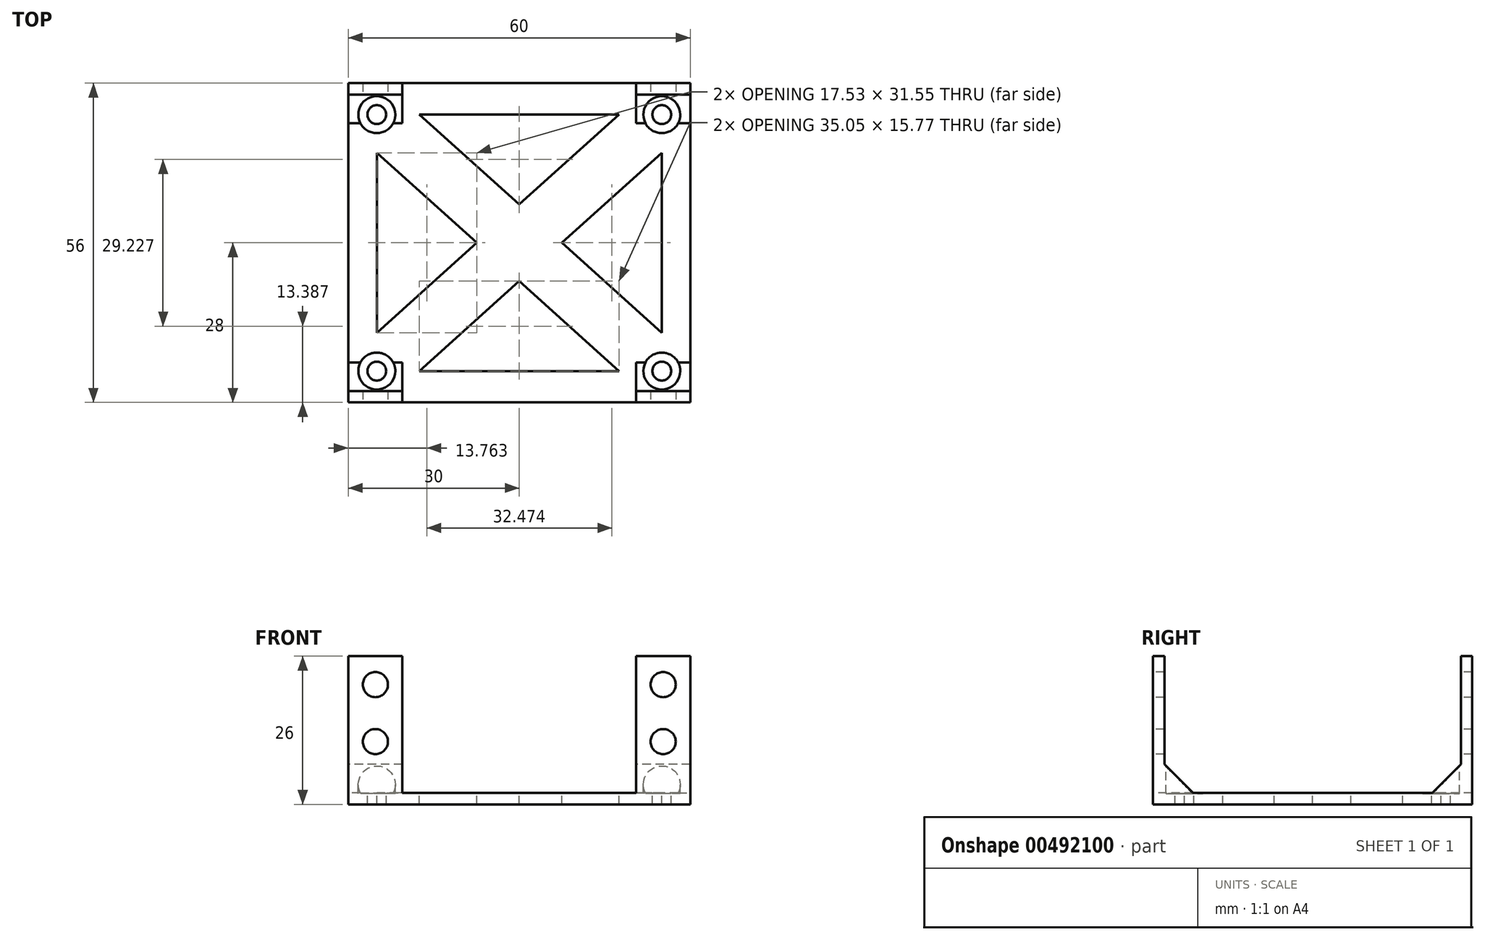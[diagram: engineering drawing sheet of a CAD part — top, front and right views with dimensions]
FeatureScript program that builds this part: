
annotation { "Feature Type Name" : "Feature", "Feature Type Description" : "" }
export const myFeature = defineFeature(function(context is Context, id is Id, definition is map)
    precondition{}
    {
        {
            var Q0;
            Q0=qCreatedBy(makeId("Top.planeOp"),FACE);
            var sketch = newSketch(context, id + "F0", { "sketchPlane" : qUnion([Q0])});
            skLineSegment(sketch, "E0.bottom", {"start": v(-30, 28) * mm, "end": v(30, 28) * mm});
            skLineSegment(sketch, "E0.top", {"start": v(-30, -28) * mm, "end": v(30, -28) * mm});
            skLineSegment(sketch, "E0.left", {"start": v(-30, 28) * mm, "end": v(-30, -28) * mm});
            skLineSegment(sketch, "E0.right", {"start": v(30, 28) * mm, "end": v(30, -28) * mm});
            skSolve(sketch);
        }
        {
            var Q0;
            Q0=makeQuery(id+"F0.imprint","IMPRINT",FACE,{"disambiguationData":[TD([[makeQuery(id+"F0.imprint","IMPRINT",EDGE,{"derivedFrom":sQuery(id+"F0.wireOp",EDGE,"E0.bottom")}),-1.0]])]});
            extrude(context, id + "F1", {"entities" : qUnion([Q0]), "depth" : 26 * mm});
        }
        {
            var Q0;
            Q0=makeQuery(id+"F1.opExtrude","SWEPT_FACE",FACE,{"disambiguationData":[OSD([sQuery(id+"F0.wireOp",EDGE,"E0.top")])]});
            var sketch = newSketch(context, id + "F2", { "sketchPlane" : qUnion([Q0])});
            skLineSegment(sketch, "E1.bottom", {"start": v(-20.5, 26) * mm, "end": v(20.5, 26) * mm});
            skLineSegment(sketch, "E1.top", {"start": v(-20.5, 2) * mm, "end": v(20.5, 2) * mm});
            skLineSegment(sketch, "E1.left", {"start": v(-20.5, 26) * mm, "end": v(-20.5, 2) * mm});
            skLineSegment(sketch, "E1.right", {"start": v(20.5, 26) * mm, "end": v(20.5, 2) * mm});
            skSolve(sketch);
        }
        {
            var Q0;
            Q0=makeQuery(id+"F2.imprint","IMPRINT",FACE,{"disambiguationData":[TD([[makeQuery(id+"F2.imprint","IMPRINT",EDGE,{"derivedFrom":sQuery(id+"F2.wireOp",EDGE,"E1.bottom")}),-1.0]])]});
            extrude(context, id + "F3", {"entities" : qUnion([Q0]), "operationType" : NewBodyOperationType.REMOVE, "endBound" : BoundingType.THROUGH_ALL, "oppositeDirection" : true, "depth" : 25 * mm});
        }
        {
            var Q0;
            Q0=makeQuery(id+"F1.opExtrude","SWEPT_FACE",FACE,{"disambiguationData":[OSD([sQuery(id+"F0.wireOp",EDGE,"E0.right")])]});
            var sketch = newSketch(context, id + "F4", { "sketchPlane" : qUnion([Q0])});
            skLineSegment(sketch, "E2.bottom", {"start": v(-26, 26) * mm, "end": v(26, 26) * mm});
            skLineSegment(sketch, "E2.top", {"start": v(-26, 2) * mm, "end": v(26, 2) * mm});
            skLineSegment(sketch, "E2.left", {"start": v(-26, 26) * mm, "end": v(-26, 2) * mm});
            skLineSegment(sketch, "E2.right", {"start": v(26, 26) * mm, "end": v(26, 2) * mm});
            skSolve(sketch);
        }
        {
            var Q0;
            Q0=makeQuery(id+"F4.imprint","IMPRINT",FACE,{"disambiguationData":[TD([[makeQuery(id+"F4.imprint","IMPRINT",EDGE,{"derivedFrom":sQuery(id+"F4.wireOp",EDGE,"E2.bottom")}),1.0]])]});
            extrude(context, id + "F5", {"entities" : qUnion([Q0]), "operationType" : NewBodyOperationType.REMOVE, "endBound" : BoundingType.THROUGH_ALL, "oppositeDirection" : true, "depth" : 25 * mm});
        }
        {
            var Q0;
            Q0=makeQuery(id+"F1.opExtrude","SWEPT_FACE",FACE,{"disambiguationData":[OSD([sQuery(id+"F0.wireOp",EDGE,"E0.top")])]});
            var sketch = newSketch(context, id + "F6", { "sketchPlane" : qUnion([Q0])});
            skPoint(sketch, "E3", {"position": v(-25.25, 21) * mm});
            skPoint(sketch, "E4", {"position": v(-25.25, 11) * mm});
            skPoint(sketch, "E5", {"position": v(25.25, 21) * mm});
            skPoint(sketch, "E6", {"position": v(25.25, 11) * mm});
            skSolve(sketch);
        }
        {
            var Q0;
            Q0=sQuery(id+"F6.wireOp",VERTEX,"E3");
            var Q1;
            Q1=sQuery(id+"F6.wireOp",VERTEX,"E5");
            var Q2;
            Q2=sQuery(id+"F6.wireOp",VERTEX,"E6");
            var Q3;
            Q3=sQuery(id+"F6.wireOp",VERTEX,"E4");
            var Q4;
            Q4=makeQuery(id+"F1.opExtrude","SWEPT_BODY",BODY,{"disambiguationData":[OSD([sQuery(id+"F0.wireOp",EDGE,"E0.bottom"),sQuery(id+"F0.wireOp",EDGE,"E0.top"),sQuery(id+"F0.wireOp",EDGE,"E0.left"),sQuery(id+"F0.wireOp",EDGE,"E0.right")])]});
            hole(context, id + "F7", {"style" : HoleStyle.SIMPLE, "endStyle" : HoleEndStyle.THROUGH, "standardTappedOrClearance" : lookupTablePath({ "standard" : "ISO", "fit" : "Normal", "size" : "M4", "type" : "Clearance" }), "standardBlindInLast" : lookupTablePath({ "fit" : "Standard", "standard" : "ISO", "size" : "M4", "type" : "Clearance" }), "holeDiameter" : 4.4 * mm, "isTappedThrough" : true, "tappedDepth" : 12 * mm, "tapClearance" : 3, "locations" : qUnion([Q0, Q1, Q2, Q3]), "scope" : qUnion([Q4])});
        }
        {
            var Q0;
            Q0=makeQuery(id+"F5.boolean.opBoolean","MERGE",FACE,{"derivedFrom":[makeQuery(id+"F3.boolean.opBoolean","COPY",FACE,{"derivedFrom":makeQuery(id+"F3.opExtrude","SWEPT_FACE",FACE,{"disambiguationData":[OSD([sQuery(id+"F2.wireOp",EDGE,"E1.top")])]})}),makeQuery(id+"F5.opExtrude","SWEPT_FACE",FACE,{"disambiguationData":[OSD([sQuery(id+"F4.wireOp",EDGE,"E2.top")])]})]});
            var sketch = newSketch(context, id + "F8", { "sketchPlane" : qUnion([Q0])});
            skPoint(sketch, "E7", {"position": v(25, 22.5) * mm});
            skPoint(sketch, "E8", {"position": v(-25, 22.5) * mm});
            skPoint(sketch, "E9", {"position": v(25, -22.5) * mm});
            skPoint(sketch, "E10", {"position": v(-25, -22.5) * mm});
            skSolve(sketch);
        }
        {
            var Q0;
            Q0=sQuery(id+"F8.wireOp",VERTEX,"E9");
            var Q1;
            Q1=sQuery(id+"F8.wireOp",VERTEX,"E10");
            var Q2;
            Q2=sQuery(id+"F8.wireOp",VERTEX,"E7");
            var Q3;
            Q3=sQuery(id+"F8.wireOp",VERTEX,"E8");
            var Q4;
            Q4=makeQuery(id+"F1.opExtrude","SWEPT_BODY",BODY,{"disambiguationData":[OSD([sQuery(id+"F0.wireOp",EDGE,"E0.bottom"),sQuery(id+"F0.wireOp",EDGE,"E0.top"),sQuery(id+"F0.wireOp",EDGE,"E0.left"),sQuery(id+"F0.wireOp",EDGE,"E0.right")])]});
            hole(context, id + "F9", {"style" : HoleStyle.C_BORE, "endStyle" : HoleEndStyle.BLIND, "holeDiameter" : 3.3 * mm, "cBoreDiameter" : 6.5 * mm, "cBoreDepth" : .1 * mm, "holeDepth" : 12 * mm, "isTappedThrough" : true, "tappedDepth" : 12 * mm, "tapClearance" : 3, "startFromSketch" : true, "locations" : qUnion([Q0, Q1, Q2, Q3]), "scope" : qUnion([Q4])});
        }
        {
            var Q0;
            Q0=makeQuery(id+"F5.boolean.opBoolean","MERGE",FACE,{"derivedFrom":[makeQuery(id+"F3.boolean.opBoolean","COPY",FACE,{"derivedFrom":makeQuery(id+"F3.opExtrude","SWEPT_FACE",FACE,{"disambiguationData":[OSD([sQuery(id+"F2.wireOp",EDGE,"E1.top")])]})}),makeQuery(id+"F5.opExtrude","SWEPT_FACE",FACE,{"disambiguationData":[OSD([sQuery(id+"F4.wireOp",EDGE,"E2.top")])]})]});
            var sketch = newSketch(context, id + "F10", { "sketchPlane" : qUnion([Q0])});
            skLineSegment(sketch, "E11", {"start": v(0, 34.63) * mm, "end": v(0, -32.5) * mm, "construction": true});
            skLineSegment(sketch, "E12", {"start": v(-36.67, 0) * mm, "end": v(41.9, 0) * mm, "construction": true});
            skLineSegment(sketch, "E13", {"start": v(-25, 22.5) * mm, "end": v(25, -22.5) * mm, "construction": true});
            skLineSegment(sketch, "E14", {"start": v(25, 22.5) * mm, "end": v(-25, -22.5) * mm, "construction": true});
            skLineSegment(sketch, "E15", {"start": v(-17.53, 22.5) * mm, "end": v(17.53, 22.5) * mm});
            skLineSegment(sketch, "E16", {"start": v(17.53, 22.5) * mm, "end": v(0, 6.73) * mm});
            skLineSegment(sketch, "E17", {"start": v(0, 6.73) * mm, "end": v(-17.53, 22.5) * mm});
            skLineSegment(sketch, "E18", {"start": v(25, 15.77) * mm, "end": v(25, -15.77) * mm});
            skLineSegment(sketch, "E19", {"start": v(25, -15.77) * mm, "end": v(7.47, 0) * mm});
            skLineSegment(sketch, "E20", {"start": v(7.47, 0) * mm, "end": v(25, 15.77) * mm});
            skLineSegment(sketch, "E21", {"start": v(-25, 15.77) * mm, "end": v(-7.47, 0) * mm});
            skLineSegment(sketch, "E22", {"start": v(-7.47, 0) * mm, "end": v(-25, -15.77) * mm});
            skLineSegment(sketch, "E23", {"start": v(-25, -15.77) * mm, "end": v(-25, 15.77) * mm});
            skLineSegment(sketch, "E24", {"start": v(-17.53, -22.5) * mm, "end": v(17.53, -22.5) * mm});
            skLineSegment(sketch, "E25", {"start": v(17.53, -22.5) * mm, "end": v(0, -6.73) * mm});
            skLineSegment(sketch, "E26", {"start": v(0, -6.73) * mm, "end": v(-17.53, -22.5) * mm});
            skSolve(sketch);
        }
        {
            var Q0;
            Q0 = qSketchRegion(id + "F10", true);
            extrude(context, id + "F11", {"entities" : qUnion([Q0]), "operationType" : NewBodyOperationType.REMOVE, "endBound" : BoundingType.THROUGH_ALL, "oppositeDirection" : true, "depth" : 25 * mm});
        }
        {
            var Q0;
            {var subQ0=sQuery(id+"F4.wireOp",EDGE,"E2.top");var subQ1=sQuery(id+"F4.wireOp",EDGE,"E2.right");Q0=makeQuery(id+"F5.boolean.opBoolean","COPY",EDGE,{"disambiguationData":[TD([makeQuery(id+"F1.opExtrude","SWEPT_FACE",FACE,{"disambiguationData":[OSD([sQuery(id+"F0.wireOp",EDGE,"E0.left")])]})])],"derivedFrom":makeQuery(id+"F5.opExtrude","SWEPT_EDGE",EDGE,{"disambiguationData":[OSD([subQ0,subQ1])]})});}
            var Q1;
            {var subQ0=sQuery(id+"F4.wireOp",EDGE,"E2.top");var subQ1=sQuery(id+"F4.wireOp",EDGE,"E2.right");Q1=makeQuery(id+"F5.boolean.opBoolean","COPY",EDGE,{"disambiguationData":[TD([makeQuery(id+"F1.opExtrude","SWEPT_FACE",FACE,{"disambiguationData":[OSD([sQuery(id+"F0.wireOp",EDGE,"E0.right")])]})])],"derivedFrom":makeQuery(id+"F5.opExtrude","SWEPT_EDGE",EDGE,{"disambiguationData":[OSD([subQ0,subQ1])]})});}
            var Q2;
            {var subQ0=sQuery(id+"F4.wireOp",EDGE,"E2.top");var subQ1=sQuery(id+"F4.wireOp",EDGE,"E2.left");Q2=makeQuery(id+"F5.boolean.opBoolean","COPY",EDGE,{"disambiguationData":[TD([makeQuery(id+"F1.opExtrude","SWEPT_FACE",FACE,{"disambiguationData":[OSD([sQuery(id+"F0.wireOp",EDGE,"E0.left")])]})])],"derivedFrom":makeQuery(id+"F5.opExtrude","SWEPT_EDGE",EDGE,{"disambiguationData":[OSD([subQ0,subQ1])]})});}
            var Q3;
            {var subQ0=sQuery(id+"F4.wireOp",EDGE,"E2.top");var subQ1=sQuery(id+"F4.wireOp",EDGE,"E2.left");Q3=makeQuery(id+"F5.boolean.opBoolean","COPY",EDGE,{"disambiguationData":[TD([makeQuery(id+"F1.opExtrude","SWEPT_FACE",FACE,{"disambiguationData":[OSD([sQuery(id+"F0.wireOp",EDGE,"E0.right")])]})])],"derivedFrom":makeQuery(id+"F5.opExtrude","SWEPT_EDGE",EDGE,{"disambiguationData":[OSD([subQ0,subQ1])]})});}
            chamfer(context, id + "F12", {"entities" : qUnion([Q0, Q1, Q2, Q3]), "width" : 5 * mm, "tangentPropagation" : true});
        }
    });
